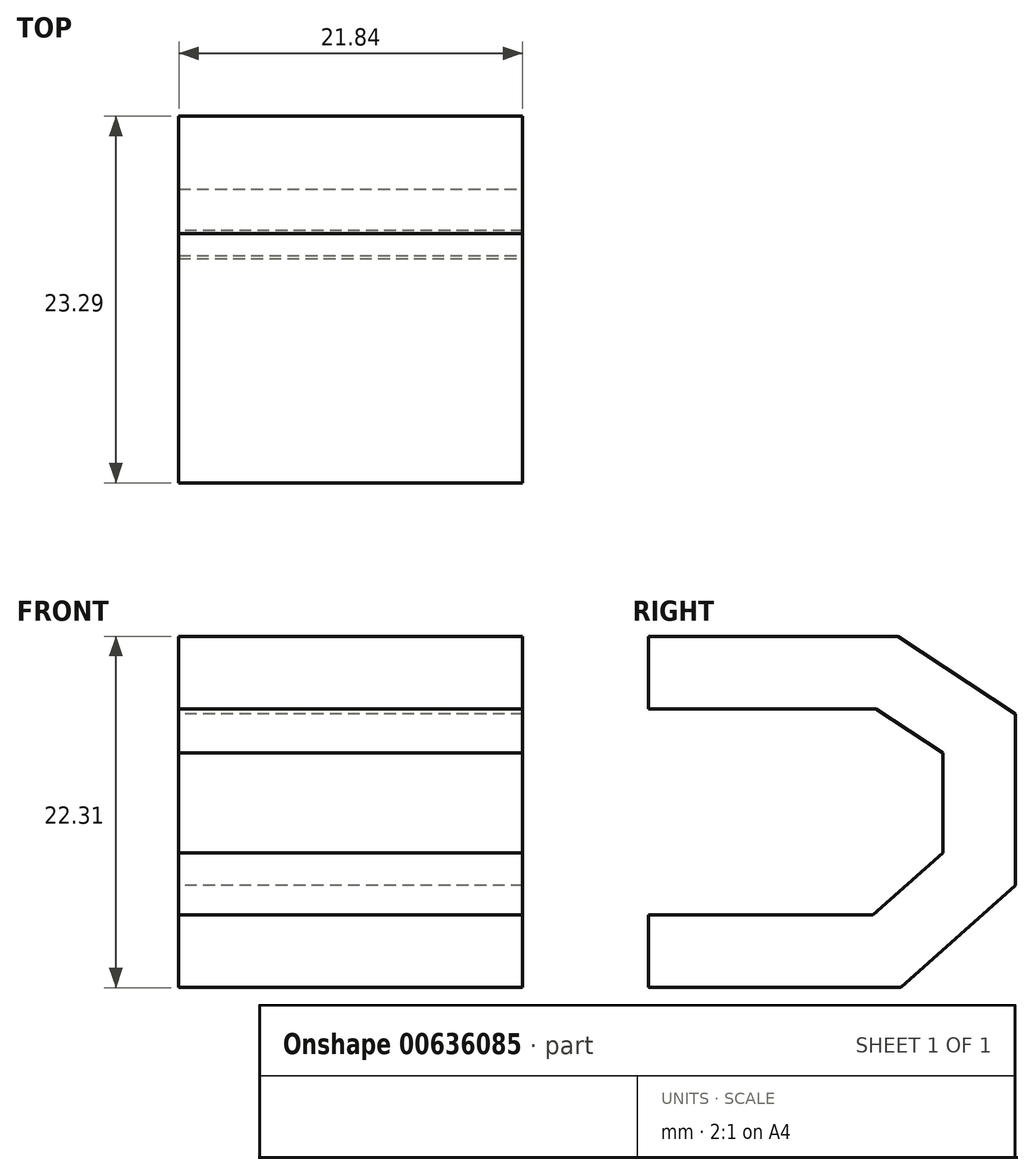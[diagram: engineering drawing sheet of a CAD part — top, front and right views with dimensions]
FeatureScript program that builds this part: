
annotation { "Feature Type Name" : "Feature", "Feature Type Description" : "" }
export const myFeature = defineFeature(function(context is Context, id is Id, definition is map)
    precondition{}
    {
        {
            var Q0;
            Q0=qCreatedBy(makeId("Front.planeOp"),FACE);
            var sketch = newSketch(context, id + "F0", { "sketchPlane" : qUnion([Q0])});
            skLineSegment(sketch, "E0.bottom", {"start": v(10.92, -2.3) * mm, "end": v(-10.92, -2.3) * mm});
            skLineSegment(sketch, "E0.top", {"start": v(10.92, 2.3) * mm, "end": v(-10.92, 2.3) * mm});
            skLineSegment(sketch, "E0.left", {"start": v(10.92, -2.3) * mm, "end": v(10.92, 2.3) * mm});
            skLineSegment(sketch, "E0.right", {"start": v(-10.92, -2.3) * mm, "end": v(-10.92, 2.3) * mm});
            skPoint(sketch, "E0.middle", {"position": v(0, 0) * mm});
            skSolve(sketch);
        }
        {
            var Q0;
            Q0=qCreatedBy(makeId("Right.planeOp"),FACE);
            var sketch = newSketch(context, id + "F1", { "sketchPlane" : qUnion([Q0])});
            skLineSegment(sketch, "E1", {"start": v(0, 0) * mm, "end": v(15.14, 0) * mm});
            skLineSegment(sketch, "E2", {"start": v(15.14, 0) * mm, "end": v(20.98, -3.85) * mm});
            skLineSegment(sketch, "E3", {"start": v(20.98, -3.85) * mm, "end": v(20.98, -12.46) * mm});
            skLineSegment(sketch, "E4", {"start": v(20.98, -12.46) * mm, "end": v(15.14, -17.69) * mm});
            skLineSegment(sketch, "E5", {"start": v(15.14, -17.69) * mm, "end": v(0, -17.69) * mm});
            skSolve(sketch);
        }
        {
            var Q0;
            Q0=makeQuery(id+"F0.imprint","IMPRINT",FACE,{"disambiguationData":[TD([[makeQuery(id+"F0.imprint","IMPRINT",EDGE,{"derivedFrom":sQuery(id+"F0.wireOp",EDGE,"E0.bottom")}),-1.0]])]});
            var Q1;
            Q1=sQuery(id+"F1.wireOp",EDGE,"E1");
            var Q2;
            Q2=sQuery(id+"F1.wireOp",EDGE,"E2");
            var Q3;
            Q3=sQuery(id+"F1.wireOp",EDGE,"E3");
            var Q4;
            Q4=sQuery(id+"F1.wireOp",EDGE,"E4");
            var Q5;
            Q5=sQuery(id+"F1.wireOp",EDGE,"E5");
            sweep(context, id + "F2", {"profiles" : qUnion([Q0]), "path" : qUnion([Q1, Q2, Q3, Q4, Q5])});
        }
    });
